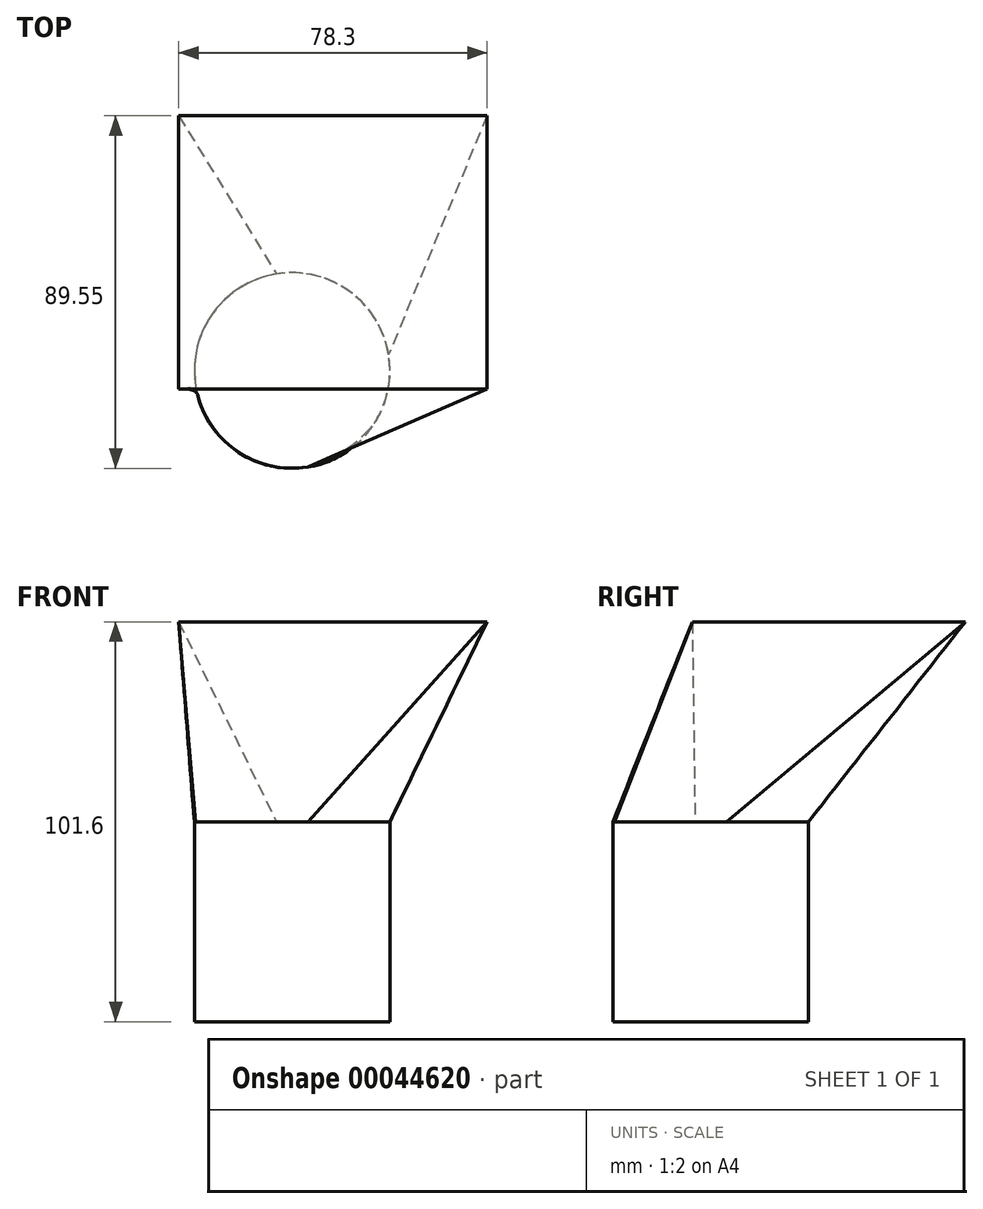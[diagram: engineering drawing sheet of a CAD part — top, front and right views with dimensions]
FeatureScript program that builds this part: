
annotation { "Feature Type Name" : "Feature", "Feature Type Description" : "" }
export const myFeature = defineFeature(function(context is Context, id is Id, definition is map)
    precondition{}
    {
        {
            var Q0;
            Q0=qCreatedBy(makeId("Top.planeOp"),FACE);
            var sketch = newSketch(context, id + "F0", { "sketchPlane" : qUnion([Q0])});
            skCircle(sketch, "E0", {"center": v(0, 0) * mm, "radius": 24.85 * mm});
            skSolve(sketch);
        }
        {
            var Q0;
            Q0=makeQuery(id+"F0.imprint","IMPRINT",FACE,{"disambiguationData":[TD([[makeQuery(id+"F0.imprint","IMPRINT",EDGE,{"derivedFrom":sQuery(id+"F0.wireOp",EDGE,"E0")}),1.0]])]});
            extrude(context, id + "F1", {"entities" : qUnion([Q0]), "depth" : 50.8 * mm});
        }
        {
            var Q0;
            Q0=makeQuery(id+"F1.opExtrude","CAP_FACE",FACE,{"disambiguationData":[OSD([sQuery(id+"F0.wireOp",EDGE,"E0")])],"isStart":false});
            var sketch = newSketch(context, id + "F2", { "sketchPlane" : qUnion([Q0])});
            skSolve(sketch);
        }
        {
            var Q0;
            Q0=qCreatedBy(makeId("Top.planeOp"),FACE);
            cPlane(context, id + "F3", {"entities" : qUnion([Q0]), "cplaneType" : CPlaneType.OFFSET, "offset" : 101.6 * mm, "width" : 152.4 * mm, "height" : 152.4 * mm});
        }
        {
            var Q0;
            Q0=qCreatedBy(id+"F3.planeOp",FACE);
            var sketch = newSketch(context, id + "F4", { "sketchPlane" : qUnion([Q0])});
            skLineSegment(sketch, "E1.bottom", {"start": v(-28.8, -4.7) * mm, "end": v(49.5, -4.7) * mm});
            skLineSegment(sketch, "E1.top", {"start": v(-28.8, 64.7) * mm, "end": v(49.5, 64.7) * mm});
            skLineSegment(sketch, "E1.left", {"start": v(-28.8, -4.7) * mm, "end": v(-28.8, 64.7) * mm});
            skLineSegment(sketch, "E1.right", {"start": v(49.5, -4.7) * mm, "end": v(49.5, 64.7) * mm});
            skSolve(sketch);
        }
        {
            var Q0;
            Q0=makeQuery(id+"F4.imprint","IMPRINT",FACE,{"disambiguationData":[TD([[makeQuery(id+"F4.imprint","IMPRINT",EDGE,{"derivedFrom":sQuery(id+"F4.wireOp",EDGE,"E1.bottom")}),1.0]])]});
            var Q1;
            Q1=makeQuery(id+"F2.imprint","IMPRINT",FACE,{"disambiguationData":[TD([[makeQuery(id+"F2.imprint","IMPRINT",EDGE,{"derivedFrom":makeQuery(id+"F1.opExtrude","CAP_EDGE",EDGE,{"disambiguationData":[OSD([sQuery(id+"F0.wireOp",EDGE,"E0")])],"isStart":false})}),1.0]])]});
            loft(context, id + "F5", {"sheetProfilesArray" : [{ "sheetProfileEntities" : qUnion([Q0]) }, { "sheetProfileEntities" : qUnion([Q1]) }]});
        }
    });
